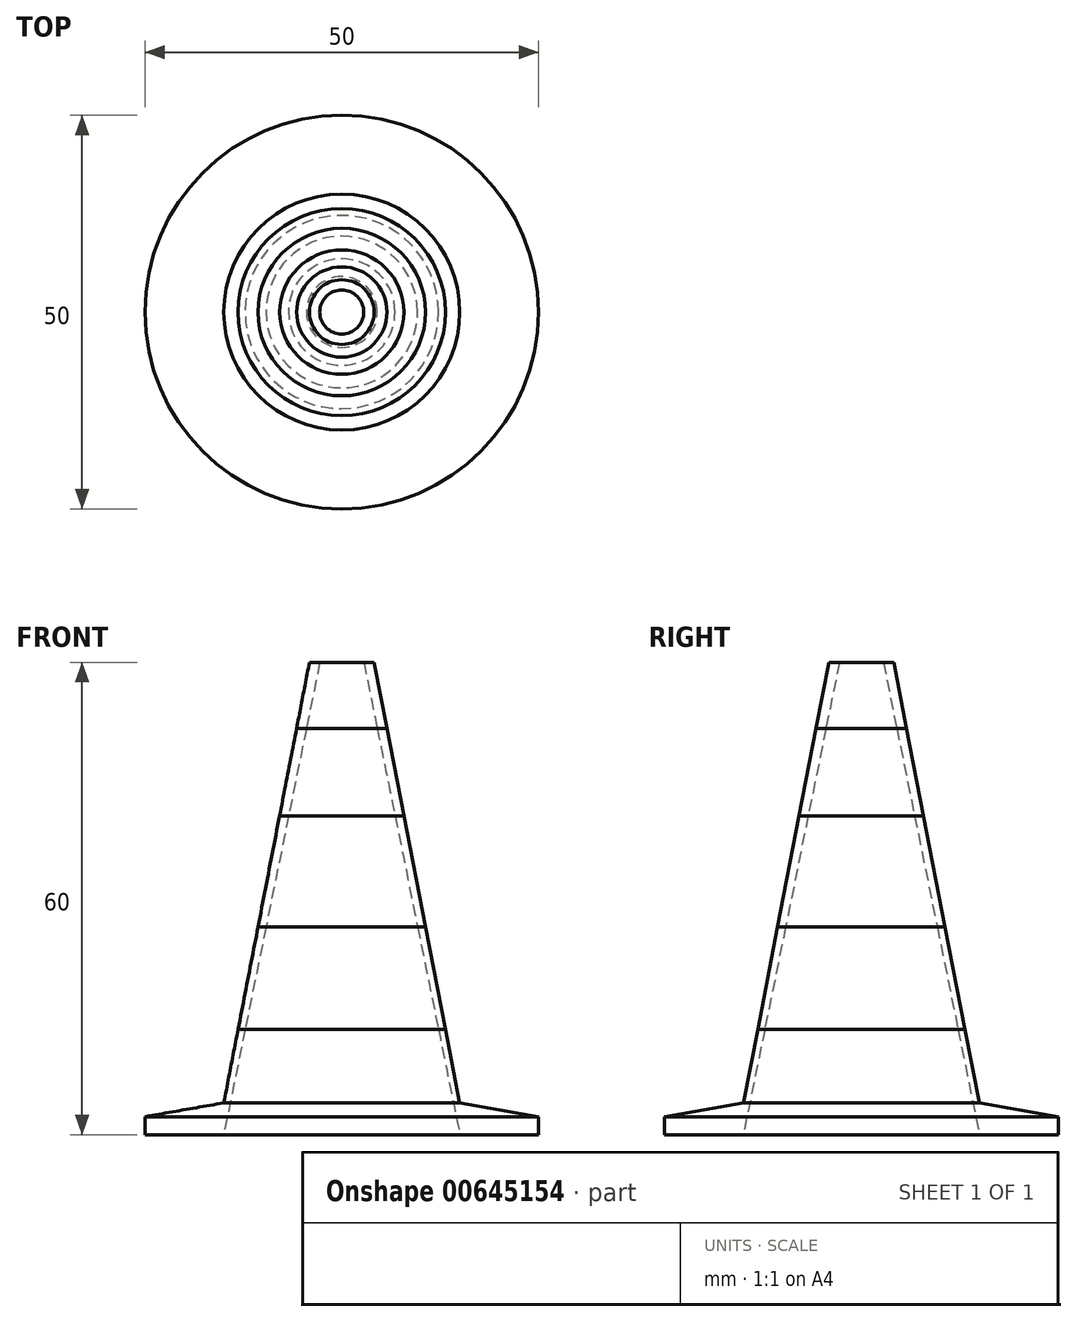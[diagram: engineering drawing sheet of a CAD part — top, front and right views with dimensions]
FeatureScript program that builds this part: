
annotation { "Feature Type Name" : "Feature", "Feature Type Description" : "" }
export const myFeature = defineFeature(function(context is Context, id is Id, definition is map)
    precondition{}
    {
        {
            var Q0;
            Q0=qCreatedBy(makeId("Front.planeOp"),FACE);
            var sketch = newSketch(context, id + "F0", { "sketchPlane" : qUnion([Q0])});
            skLineSegment(sketch, "E0", {"start": v(0, 0) * mm, "end": v(-25, 0) * mm});
            skLineSegment(sketch, "E1", {"start": v(0, 0) * mm, "end": v(0, 60) * mm});
            skLineSegment(sketch, "E2", {"start": v(-25, 0) * mm, "end": v(-25, 2.28) * mm});
            skLineSegment(sketch, "E3", {"start": v(-25, 2.28) * mm, "end": v(-14.98, 4.05) * mm});
            skLineSegment(sketch, "E4", {"start": v(-14.98, 4.05) * mm, "end": v(-4.1, 60) * mm});
            skLineSegment(sketch, "E5", {"start": v(-4.1, 60) * mm, "end": v(0, 60) * mm});
            skLineSegment(sketch, "E6", {"start": v(-13.17, 13.4) * mm, "end": v(0, 13.4) * mm});
            skLineSegment(sketch, "E7", {"start": v(-10.64, 26.4) * mm, "end": v(0, 26.4) * mm});
            skLineSegment(sketch, "E8", {"start": v(-7.9, 40.5) * mm, "end": v(0, 40.5) * mm});
            skLineSegment(sketch, "E9", {"start": v(-5.74, 51.6) * mm, "end": v(0, 51.6) * mm});
            skSolve(sketch);
        }
        {
            var Q0;
            {var subQ0=sQuery(id+"F0.wireOp",EDGE,"E8");Q0=makeQuery(id+"F0.imprint","IMPRINT",FACE,{"disambiguationData":[TD([[makeQuery(id+"F0.imprint","IMPRINT",EDGE,{"derivedFrom":subQ0}),1.0]])]});}
            var Q1;
            Q1=sQuery(id+"F0.wireOp",EDGE,"E1");
            revolve(context, id + "F1", {"entities" : qUnion([Q0]), "axis" : qUnion([Q1]), "revolveType" : RevolveType.FULL});
        }
        {
            var Q0;
            {var subQ0=sQuery(id+"F0.wireOp",EDGE,"E5");Q0=makeQuery(id+"F0.imprint","IMPRINT",FACE,{"disambiguationData":[TD([[makeQuery(id+"F0.imprint","IMPRINT",EDGE,{"derivedFrom":subQ0}),-1.0]])]});}
            var Q1;
            Q1=sQuery(id+"F0.wireOp",EDGE,"E1");
            revolve(context, id + "F2", {"entities" : qUnion([Q0]), "axis" : qUnion([Q1]), "revolveType" : RevolveType.FULL});
        }
        {
            var Q0;
            {var subQ0=sQuery(id+"F0.wireOp",EDGE,"E7");Q0=makeQuery(id+"F0.imprint","IMPRINT",FACE,{"disambiguationData":[TD([[makeQuery(id+"F0.imprint","IMPRINT",EDGE,{"derivedFrom":subQ0}),1.0]])]});}
            var Q1;
            Q1=sQuery(id+"F0.wireOp",EDGE,"E1");
            revolve(context, id + "F3", {"entities" : qUnion([Q0]), "axis" : qUnion([Q1]), "revolveType" : RevolveType.FULL});
        }
        {
            var Q0;
            {var subQ0=sQuery(id+"F0.wireOp",EDGE,"E6");Q0=makeQuery(id+"F0.imprint","IMPRINT",FACE,{"disambiguationData":[TD([[makeQuery(id+"F0.imprint","IMPRINT",EDGE,{"derivedFrom":subQ0}),1.0]])]});}
            var Q1;
            Q1=sQuery(id+"F0.wireOp",EDGE,"E1");
            revolve(context, id + "F4", {"entities" : qUnion([Q0]), "axis" : qUnion([Q1]), "revolveType" : RevolveType.FULL});
        }
        {
            var Q0;
            {var subQ2=sQuery(id+"F0.wireOp",EDGE,"E0");Q0=makeQuery(id+"F0.imprint","IMPRINT",FACE,{"disambiguationData":[TD([[makeQuery(id+"F0.imprint","IMPRINT",EDGE,{"derivedFrom":subQ2}),-1.0]])]});}
            var Q1;
            Q1=sQuery(id+"F0.wireOp",EDGE,"E1");
            revolve(context, id + "F5", {"entities" : qUnion([Q0]), "axis" : qUnion([Q1]), "revolveType" : RevolveType.FULL});
        }
        {
            var Q0;
            Q0=makeQuery(id+"F5.opRevolve","SWEPT_FACE",FACE,{"disambiguationData":[OSD([sQuery(id+"F0.wireOp",EDGE,"E0")])]});
            var sketch = newSketch(context, id + "F6", { "sketchPlane" : qUnion([Q0])});
            skCircle(sketch, "E10", {"center": v(0, 0) * mm, "radius": 15 * mm});
            skSolve(sketch);
        }
        {
            var Q0;
            Q0=makeQuery(id+"F6.imprint","IMPRINT",FACE,{"disambiguationData":[TD([[makeQuery(id+"F6.imprint","IMPRINT",EDGE,{"derivedFrom":sQuery(id+"F6.wireOp",EDGE,"E10")}),1.0]])]});
            extrude(context, id + "F7", {"entities" : qUnion([Q0]), "operationType" : NewBodyOperationType.REMOVE, "endBound" : BoundingType.THROUGH_ALL, "oppositeDirection" : true, "depth" : 25 * mm, "offsetDistance" : 25 * mm, "hasDraft" : true, "draftAngle" : 11.5 * degree, "draftPullDirection" : true});
        }
    });
